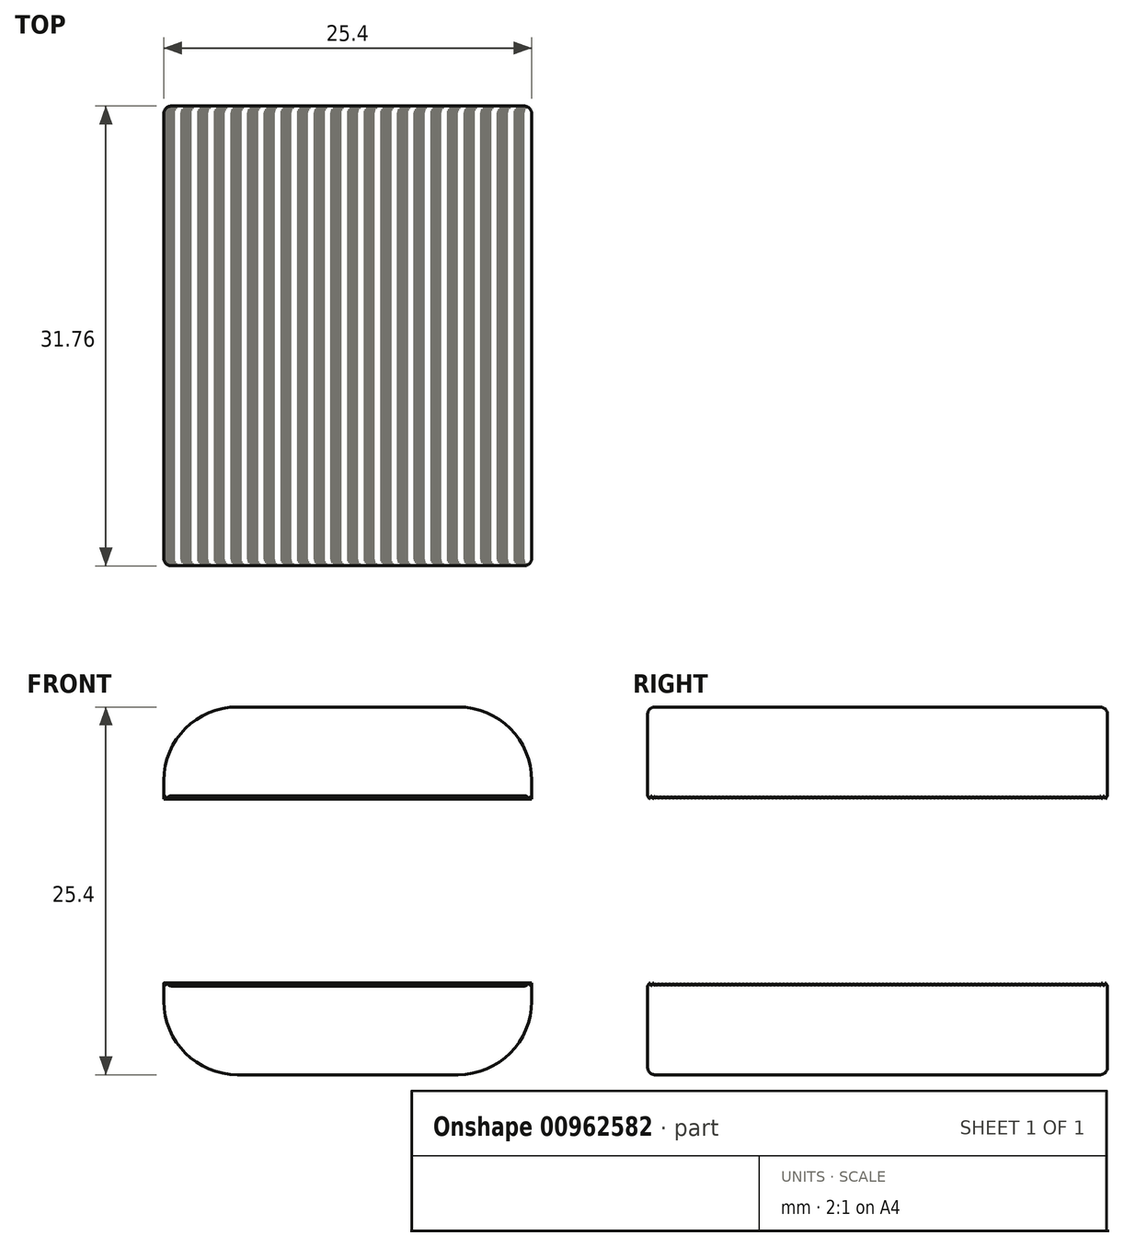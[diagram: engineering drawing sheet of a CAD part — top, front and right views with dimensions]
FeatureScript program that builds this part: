
annotation { "Feature Type Name" : "Feature", "Feature Type Description" : "" }
export const myFeature = defineFeature(function(context is Context, id is Id, definition is map)
    precondition{}
    {
        {
            var Q0;
            Q0=qCreatedBy(makeId("Front.planeOp"),FACE);
            var sketch = newSketch(context, id + "F0", { "sketchPlane" : qUnion([Q0])});
            skLineSegment(sketch, "E0.bottom", {"start": v(12.7, -12.7) * mm, "end": v(-12.7, -12.7) * mm});
            skLineSegment(sketch, "E0.top", {"start": v(12.7, 12.7) * mm, "end": v(-12.7, 12.7) * mm});
            skLineSegment(sketch, "E0.left", {"start": v(12.7, -12.7) * mm, "end": v(12.7, -6.35) * mm});
            skLineSegment(sketch, "E0.right", {"start": v(-12.7, -12.7) * mm, "end": v(-12.7, -6.35) * mm});
            skPoint(sketch, "E0.middle", {"position": v(0, 0) * mm});
            skLineSegment(sketch, "E1.bottom", {"start": v(12.7, -6.35) * mm, "end": v(-12.7, -6.35) * mm});
            skLineSegment(sketch, "E1.top", {"start": v(12.7, 6.35) * mm, "end": v(-12.7, 6.35) * mm});
            skLineSegment(sketch, "E2.trimOffspring", {"start": v(-12.7, 6.35) * mm, "end": v(-12.7, 12.7) * mm});
            skLineSegment(sketch, "E3.trimOffspring", {"start": v(12.7, 6.35) * mm, "end": v(12.7, 12.7) * mm});
            skSolve(sketch);
        }
        {
            var Q0;
            Q0 = qSketchRegion(id + "F0", true);
            extrude(context, id + "F1", {"entities" : qUnion([Q0]), "endBound" : BoundingType.SYMMETRIC, "depth" : 31.75 * mm, "offsetDistance" : 25.4 * mm});
        }
        {
            var Q0;
            Q0=qCreatedBy(makeId("Right.planeOp"),FACE);
            var sketch = newSketch(context, id + "F2", { "sketchPlane" : qUnion([Q0])});
            skLineSegment(sketch, "E4", {"start": v(0, 6.35) * mm, "end": v(-0.13, 6.57) * mm});
            skLineSegment(sketch, "E5", {"start": v(-0.13, 6.57) * mm, "end": v(-0.25, 6.35) * mm});
            skLineSegment(sketch, "E6.1.0.0", {"start": v(-0.25, 6.35) * mm, "end": v(-0.38, 6.57) * mm});
            skLineSegment(sketch, "E6.1.0.1", {"start": v(-0.38, 6.57) * mm, "end": v(-0.5, 6.35) * mm});
            skLineSegment(sketch, "E6.2.0.0", {"start": v(-0.5, 6.35) * mm, "end": v(-0.64, 6.57) * mm});
            skLineSegment(sketch, "E6.2.0.1", {"start": v(-0.64, 6.57) * mm, "end": v(-0.76, 6.35) * mm});
            skLineSegment(sketch, "E6.3.0.0", {"start": v(-0.76, 6.35) * mm, "end": v(-0.89, 6.57) * mm});
            skLineSegment(sketch, "E6.3.0.1", {"start": v(-0.89, 6.57) * mm, "end": v(-1.02, 6.35) * mm});
            skLineSegment(sketch, "E6.4.0.0", {"start": v(-1.02, 6.35) * mm, "end": v(-1.14, 6.57) * mm});
            skLineSegment(sketch, "E6.4.0.1", {"start": v(-1.14, 6.57) * mm, "end": v(-1.27, 6.35) * mm});
            skLineSegment(sketch, "E6.5.0.0", {"start": v(-1.27, 6.35) * mm, "end": v(-1.4, 6.57) * mm});
            skLineSegment(sketch, "E6.5.0.1", {"start": v(-1.4, 6.57) * mm, "end": v(-1.52, 6.35) * mm});
            skLineSegment(sketch, "E6.6.0.0", {"start": v(-1.52, 6.35) * mm, "end": v(-1.65, 6.57) * mm});
            skLineSegment(sketch, "E6.6.0.1", {"start": v(-1.65, 6.57) * mm, "end": v(-1.78, 6.35) * mm});
            skLineSegment(sketch, "E6.7.0.0", {"start": v(-1.78, 6.35) * mm, "end": v(-1.9, 6.57) * mm});
            skLineSegment(sketch, "E6.7.0.1", {"start": v(-1.9, 6.57) * mm, "end": v(-2.03, 6.35) * mm});
            skLineSegment(sketch, "E6.8.0.0", {"start": v(-2.03, 6.35) * mm, "end": v(-2.16, 6.57) * mm});
            skLineSegment(sketch, "E6.8.0.1", {"start": v(-2.16, 6.57) * mm, "end": v(-2.29, 6.35) * mm});
            skLineSegment(sketch, "E6.9.0.0", {"start": v(-2.29, 6.35) * mm, "end": v(-2.41, 6.57) * mm});
            skLineSegment(sketch, "E6.9.0.1", {"start": v(-2.41, 6.57) * mm, "end": v(-2.54, 6.35) * mm});
            skLineSegment(sketch, "E6.10.0.0", {"start": v(-2.54, 6.35) * mm, "end": v(-2.67, 6.57) * mm});
            skLineSegment(sketch, "E6.10.0.1", {"start": v(-2.67, 6.57) * mm, "end": v(-2.8, 6.35) * mm});
            skLineSegment(sketch, "E6.11.0.0", {"start": v(-2.8, 6.35) * mm, "end": v(-2.92, 6.57) * mm});
            skLineSegment(sketch, "E6.11.0.1", {"start": v(-2.92, 6.57) * mm, "end": v(-3.05, 6.35) * mm});
            skLineSegment(sketch, "E6.12.0.0", {"start": v(-3.05, 6.35) * mm, "end": v(-3.18, 6.57) * mm});
            skLineSegment(sketch, "E6.12.0.1", {"start": v(-3.18, 6.57) * mm, "end": v(-3.3, 6.35) * mm});
            skLineSegment(sketch, "E6.13.0.0", {"start": v(-3.3, 6.35) * mm, "end": v(-3.43, 6.57) * mm});
            skLineSegment(sketch, "E6.13.0.1", {"start": v(-3.43, 6.57) * mm, "end": v(-3.56, 6.35) * mm});
            skLineSegment(sketch, "E6.14.0.0", {"start": v(-3.56, 6.35) * mm, "end": v(-3.68, 6.57) * mm});
            skLineSegment(sketch, "E6.14.0.1", {"start": v(-3.68, 6.57) * mm, "end": v(-3.81, 6.35) * mm});
            skLineSegment(sketch, "E6.15.0.0", {"start": v(-3.81, 6.35) * mm, "end": v(-3.94, 6.57) * mm});
            skLineSegment(sketch, "E6.15.0.1", {"start": v(-3.94, 6.57) * mm, "end": v(-4.06, 6.35) * mm});
            skLineSegment(sketch, "E6.16.0.0", {"start": v(-4.06, 6.35) * mm, "end": v(-4.2, 6.57) * mm});
            skLineSegment(sketch, "E6.16.0.1", {"start": v(-4.2, 6.57) * mm, "end": v(-4.32, 6.35) * mm});
            skLineSegment(sketch, "E6.17.0.0", {"start": v(-4.32, 6.35) * mm, "end": v(-4.45, 6.57) * mm});
            skLineSegment(sketch, "E6.17.0.1", {"start": v(-4.45, 6.57) * mm, "end": v(-4.57, 6.35) * mm});
            skLineSegment(sketch, "E6.18.0.0", {"start": v(-4.57, 6.35) * mm, "end": v(-4.7, 6.57) * mm});
            skLineSegment(sketch, "E6.18.0.1", {"start": v(-4.7, 6.57) * mm, "end": v(-4.83, 6.35) * mm});
            skLineSegment(sketch, "E6.19.0.0", {"start": v(-4.83, 6.35) * mm, "end": v(-4.95, 6.57) * mm});
            skLineSegment(sketch, "E6.19.0.1", {"start": v(-4.95, 6.57) * mm, "end": v(-5.08, 6.35) * mm});
            skLineSegment(sketch, "E6.20.0.0", {"start": v(-5.08, 6.35) * mm, "end": v(-5.2, 6.57) * mm});
            skLineSegment(sketch, "E6.20.0.1", {"start": v(-5.2, 6.57) * mm, "end": v(-5.33, 6.35) * mm});
            skLineSegment(sketch, "E6.21.0.0", {"start": v(-5.33, 6.35) * mm, "end": v(-5.46, 6.57) * mm});
            skLineSegment(sketch, "E6.21.0.1", {"start": v(-5.46, 6.57) * mm, "end": v(-5.59, 6.35) * mm});
            skLineSegment(sketch, "E6.22.0.0", {"start": v(-5.59, 6.35) * mm, "end": v(-5.72, 6.57) * mm});
            skLineSegment(sketch, "E6.22.0.1", {"start": v(-5.72, 6.57) * mm, "end": v(-5.84, 6.35) * mm});
            skLineSegment(sketch, "E6.23.0.0", {"start": v(-5.84, 6.35) * mm, "end": v(-5.97, 6.57) * mm});
            skLineSegment(sketch, "E6.23.0.1", {"start": v(-5.97, 6.57) * mm, "end": v(-6.1, 6.35) * mm});
            skLineSegment(sketch, "E6.24.0.0", {"start": v(-6.1, 6.35) * mm, "end": v(-6.22, 6.57) * mm});
            skLineSegment(sketch, "E6.24.0.1", {"start": v(-6.22, 6.57) * mm, "end": v(-6.35, 6.35) * mm});
            skLineSegment(sketch, "E6.direction1", {"start": v(-0.25, 6.35) * mm, "end": v(-0.5, 6.35) * mm, "construction": true});
            skLineSegment(sketch, "E7.0.25.0", {"start": v(-6.35, 6.35) * mm, "end": v(-6.48, 6.57) * mm});
            skLineSegment(sketch, "E7.3.25.0", {"start": v(-6.48, 6.57) * mm, "end": v(-6.6, 6.35) * mm});
            skLineSegment(sketch, "E7.0.26.0", {"start": v(-6.6, 6.35) * mm, "end": v(-6.73, 6.57) * mm});
            skLineSegment(sketch, "E7.3.26.0", {"start": v(-6.73, 6.57) * mm, "end": v(-6.86, 6.35) * mm});
            skLineSegment(sketch, "E7.0.27.0", {"start": v(-6.86, 6.35) * mm, "end": v(-6.99, 6.57) * mm});
            skLineSegment(sketch, "E7.3.27.0", {"start": v(-6.99, 6.57) * mm, "end": v(-7.11, 6.35) * mm});
            skLineSegment(sketch, "E7.0.28.0", {"start": v(-7.11, 6.35) * mm, "end": v(-7.24, 6.57) * mm});
            skLineSegment(sketch, "E7.3.28.0", {"start": v(-7.24, 6.57) * mm, "end": v(-7.37, 6.35) * mm});
            skLineSegment(sketch, "E7.0.29.0", {"start": v(-7.37, 6.35) * mm, "end": v(-7.5, 6.57) * mm});
            skLineSegment(sketch, "E7.3.29.0", {"start": v(-7.5, 6.57) * mm, "end": v(-7.62, 6.35) * mm});
            skLineSegment(sketch, "E7.0.30.0", {"start": v(-7.62, 6.35) * mm, "end": v(-7.75, 6.57) * mm});
            skLineSegment(sketch, "E7.3.30.0", {"start": v(-7.75, 6.57) * mm, "end": v(-7.87, 6.35) * mm});
            skLineSegment(sketch, "E7.0.31.0", {"start": v(-7.87, 6.35) * mm, "end": v(-8, 6.57) * mm});
            skLineSegment(sketch, "E7.3.31.0", {"start": v(-8, 6.57) * mm, "end": v(-8.13, 6.35) * mm});
            skLineSegment(sketch, "E7.0.32.0", {"start": v(-8.13, 6.35) * mm, "end": v(-8.26, 6.57) * mm});
            skLineSegment(sketch, "E7.3.32.0", {"start": v(-8.26, 6.57) * mm, "end": v(-8.38, 6.35) * mm});
            skLineSegment(sketch, "E7.0.33.0", {"start": v(-8.38, 6.35) * mm, "end": v(-8.5, 6.57) * mm});
            skLineSegment(sketch, "E7.3.33.0", {"start": v(-8.5, 6.57) * mm, "end": v(-8.64, 6.35) * mm});
            skLineSegment(sketch, "E7.0.34.0", {"start": v(-8.64, 6.35) * mm, "end": v(-8.76, 6.57) * mm});
            skLineSegment(sketch, "E7.3.34.0", {"start": v(-8.76, 6.57) * mm, "end": v(-8.9, 6.35) * mm});
            skLineSegment(sketch, "E7.0.35.0", {"start": v(-8.9, 6.35) * mm, "end": v(-9.02, 6.57) * mm});
            skLineSegment(sketch, "E7.3.35.0", {"start": v(-9.02, 6.57) * mm, "end": v(-9.14, 6.35) * mm});
            skLineSegment(sketch, "E7.0.36.0", {"start": v(-9.14, 6.35) * mm, "end": v(-9.27, 6.57) * mm});
            skLineSegment(sketch, "E7.3.36.0", {"start": v(-9.27, 6.57) * mm, "end": v(-9.4, 6.35) * mm});
            skLineSegment(sketch, "E7.0.37.0", {"start": v(-9.4, 6.35) * mm, "end": v(-9.53, 6.57) * mm});
            skLineSegment(sketch, "E7.3.37.0", {"start": v(-9.53, 6.57) * mm, "end": v(-9.65, 6.35) * mm});
            skLineSegment(sketch, "E7.0.38.0", {"start": v(-9.65, 6.35) * mm, "end": v(-9.78, 6.57) * mm});
            skLineSegment(sketch, "E7.3.38.0", {"start": v(-9.78, 6.57) * mm, "end": v(-9.9, 6.35) * mm});
            skLineSegment(sketch, "E7.0.39.0", {"start": v(-9.9, 6.35) * mm, "end": v(-10.03, 6.57) * mm});
            skLineSegment(sketch, "E7.3.39.0", {"start": v(-10.03, 6.57) * mm, "end": v(-10.16, 6.35) * mm});
            skLineSegment(sketch, "E8.1.0.0", {"start": v(0.13, 6.57) * mm, "end": v(0, 6.35) * mm});
            skLineSegment(sketch, "E8.1.0.1", {"start": v(0.25, 6.35) * mm, "end": v(0.13, 6.57) * mm});
            skLineSegment(sketch, "E8.2.0.0", {"start": v(0.38, 6.57) * mm, "end": v(0.25, 6.35) * mm});
            skLineSegment(sketch, "E8.2.0.1", {"start": v(0.5, 6.35) * mm, "end": v(0.38, 6.57) * mm});
            skLineSegment(sketch, "E8.3.0.0", {"start": v(0.64, 6.57) * mm, "end": v(0.5, 6.35) * mm});
            skLineSegment(sketch, "E8.3.0.1", {"start": v(0.76, 6.35) * mm, "end": v(0.63, 6.57) * mm});
            skLineSegment(sketch, "E8.4.0.0", {"start": v(0.89, 6.57) * mm, "end": v(0.76, 6.35) * mm});
            skLineSegment(sketch, "E8.4.0.1", {"start": v(1.02, 6.35) * mm, "end": v(0.89, 6.57) * mm});
            skLineSegment(sketch, "E8.5.0.0", {"start": v(1.14, 6.57) * mm, "end": v(1.02, 6.35) * mm});
            skLineSegment(sketch, "E8.5.0.1", {"start": v(1.27, 6.35) * mm, "end": v(1.14, 6.57) * mm});
            skLineSegment(sketch, "E8.6.0.0", {"start": v(1.4, 6.57) * mm, "end": v(1.27, 6.35) * mm});
            skLineSegment(sketch, "E8.6.0.1", {"start": v(1.52, 6.35) * mm, "end": v(1.4, 6.57) * mm});
            skLineSegment(sketch, "E8.7.0.0", {"start": v(1.65, 6.57) * mm, "end": v(1.52, 6.35) * mm});
            skLineSegment(sketch, "E8.7.0.1", {"start": v(1.78, 6.35) * mm, "end": v(1.65, 6.57) * mm});
            skLineSegment(sketch, "E8.8.0.0", {"start": v(1.9, 6.57) * mm, "end": v(1.78, 6.35) * mm});
            skLineSegment(sketch, "E8.8.0.1", {"start": v(2.03, 6.35) * mm, "end": v(1.9, 6.57) * mm});
            skLineSegment(sketch, "E8.9.0.0", {"start": v(2.16, 6.57) * mm, "end": v(2.03, 6.35) * mm});
            skLineSegment(sketch, "E8.9.0.1", {"start": v(2.29, 6.35) * mm, "end": v(2.16, 6.57) * mm});
            skLineSegment(sketch, "E8.10.0.0", {"start": v(2.41, 6.57) * mm, "end": v(2.29, 6.35) * mm});
            skLineSegment(sketch, "E8.10.0.1", {"start": v(2.54, 6.35) * mm, "end": v(2.41, 6.57) * mm});
            skLineSegment(sketch, "E8.11.0.0", {"start": v(2.67, 6.57) * mm, "end": v(2.54, 6.35) * mm});
            skLineSegment(sketch, "E8.11.0.1", {"start": v(2.8, 6.35) * mm, "end": v(2.67, 6.57) * mm});
            skLineSegment(sketch, "E8.12.0.0", {"start": v(2.92, 6.57) * mm, "end": v(2.8, 6.35) * mm});
            skLineSegment(sketch, "E8.12.0.1", {"start": v(3.05, 6.35) * mm, "end": v(2.92, 6.57) * mm});
            skLineSegment(sketch, "E8.13.0.0", {"start": v(3.18, 6.57) * mm, "end": v(3.05, 6.35) * mm});
            skLineSegment(sketch, "E8.13.0.1", {"start": v(3.3, 6.35) * mm, "end": v(3.18, 6.57) * mm});
            skLineSegment(sketch, "E8.14.0.0", {"start": v(3.43, 6.57) * mm, "end": v(3.3, 6.35) * mm});
            skLineSegment(sketch, "E8.14.0.1", {"start": v(3.56, 6.35) * mm, "end": v(3.43, 6.57) * mm});
            skLineSegment(sketch, "E8.15.0.0", {"start": v(3.68, 6.57) * mm, "end": v(3.56, 6.35) * mm});
            skLineSegment(sketch, "E8.15.0.1", {"start": v(3.81, 6.35) * mm, "end": v(3.68, 6.57) * mm});
            skLineSegment(sketch, "E8.16.0.0", {"start": v(3.94, 6.57) * mm, "end": v(3.81, 6.35) * mm});
            skLineSegment(sketch, "E8.16.0.1", {"start": v(4.06, 6.35) * mm, "end": v(3.94, 6.57) * mm});
            skLineSegment(sketch, "E8.17.0.0", {"start": v(4.2, 6.57) * mm, "end": v(4.06, 6.35) * mm});
            skLineSegment(sketch, "E8.17.0.1", {"start": v(4.32, 6.35) * mm, "end": v(4.2, 6.57) * mm});
            skLineSegment(sketch, "E8.18.0.0", {"start": v(4.45, 6.57) * mm, "end": v(4.32, 6.35) * mm});
            skLineSegment(sketch, "E8.18.0.1", {"start": v(4.57, 6.35) * mm, "end": v(4.45, 6.57) * mm});
            skLineSegment(sketch, "E8.19.0.0", {"start": v(4.7, 6.57) * mm, "end": v(4.57, 6.35) * mm});
            skLineSegment(sketch, "E8.19.0.1", {"start": v(4.83, 6.35) * mm, "end": v(4.7, 6.57) * mm});
            skLineSegment(sketch, "E8.20.0.0", {"start": v(4.95, 6.57) * mm, "end": v(4.83, 6.35) * mm});
            skLineSegment(sketch, "E8.20.0.1", {"start": v(5.08, 6.35) * mm, "end": v(4.95, 6.57) * mm});
            skLineSegment(sketch, "E8.21.0.0", {"start": v(5.2, 6.57) * mm, "end": v(5.08, 6.35) * mm});
            skLineSegment(sketch, "E8.21.0.1", {"start": v(5.33, 6.35) * mm, "end": v(5.2, 6.57) * mm});
            skLineSegment(sketch, "E8.22.0.0", {"start": v(5.46, 6.57) * mm, "end": v(5.33, 6.35) * mm});
            skLineSegment(sketch, "E8.22.0.1", {"start": v(5.59, 6.35) * mm, "end": v(5.46, 6.57) * mm});
            skLineSegment(sketch, "E8.23.0.0", {"start": v(5.72, 6.57) * mm, "end": v(5.59, 6.35) * mm});
            skLineSegment(sketch, "E8.23.0.1", {"start": v(5.84, 6.35) * mm, "end": v(5.72, 6.57) * mm});
            skLineSegment(sketch, "E8.24.0.0", {"start": v(5.97, 6.57) * mm, "end": v(5.84, 6.35) * mm});
            skLineSegment(sketch, "E8.24.0.1", {"start": v(6.1, 6.35) * mm, "end": v(5.97, 6.57) * mm});
            skLineSegment(sketch, "E8.25.0.0", {"start": v(6.22, 6.57) * mm, "end": v(6.1, 6.35) * mm});
            skLineSegment(sketch, "E8.25.0.1", {"start": v(6.35, 6.35) * mm, "end": v(6.22, 6.57) * mm});
            skLineSegment(sketch, "E8.26.0.0", {"start": v(6.48, 6.57) * mm, "end": v(6.35, 6.35) * mm});
            skLineSegment(sketch, "E8.26.0.1", {"start": v(6.6, 6.35) * mm, "end": v(6.48, 6.57) * mm});
            skLineSegment(sketch, "E8.27.0.0", {"start": v(6.73, 6.57) * mm, "end": v(6.6, 6.35) * mm});
            skLineSegment(sketch, "E8.27.0.1", {"start": v(6.86, 6.35) * mm, "end": v(6.73, 6.57) * mm});
            skLineSegment(sketch, "E8.28.0.0", {"start": v(6.99, 6.57) * mm, "end": v(6.86, 6.35) * mm});
            skLineSegment(sketch, "E8.28.0.1", {"start": v(7.11, 6.35) * mm, "end": v(6.99, 6.57) * mm});
            skLineSegment(sketch, "E8.29.0.0", {"start": v(7.24, 6.57) * mm, "end": v(7.11, 6.35) * mm});
            skLineSegment(sketch, "E8.29.0.1", {"start": v(7.37, 6.35) * mm, "end": v(7.24, 6.57) * mm});
            skLineSegment(sketch, "E8.30.0.0", {"start": v(7.5, 6.57) * mm, "end": v(7.37, 6.35) * mm});
            skLineSegment(sketch, "E8.30.0.1", {"start": v(7.62, 6.35) * mm, "end": v(7.5, 6.57) * mm});
            skLineSegment(sketch, "E8.31.0.0", {"start": v(7.75, 6.57) * mm, "end": v(7.62, 6.35) * mm});
            skLineSegment(sketch, "E8.31.0.1", {"start": v(7.87, 6.35) * mm, "end": v(7.75, 6.57) * mm});
            skLineSegment(sketch, "E8.32.0.0", {"start": v(8, 6.57) * mm, "end": v(7.87, 6.35) * mm});
            skLineSegment(sketch, "E8.32.0.1", {"start": v(8.13, 6.35) * mm, "end": v(8, 6.57) * mm});
            skLineSegment(sketch, "E8.33.0.0", {"start": v(8.26, 6.57) * mm, "end": v(8.13, 6.35) * mm});
            skLineSegment(sketch, "E8.33.0.1", {"start": v(8.38, 6.35) * mm, "end": v(8.26, 6.57) * mm});
            skLineSegment(sketch, "E8.34.0.0", {"start": v(8.5, 6.57) * mm, "end": v(8.38, 6.35) * mm});
            skLineSegment(sketch, "E8.34.0.1", {"start": v(8.64, 6.35) * mm, "end": v(8.5, 6.57) * mm});
            skLineSegment(sketch, "E8.35.0.0", {"start": v(8.76, 6.57) * mm, "end": v(8.64, 6.35) * mm});
            skLineSegment(sketch, "E8.35.0.1", {"start": v(8.9, 6.35) * mm, "end": v(8.76, 6.57) * mm});
            skLineSegment(sketch, "E8.36.0.0", {"start": v(9.02, 6.57) * mm, "end": v(8.9, 6.35) * mm});
            skLineSegment(sketch, "E8.36.0.1", {"start": v(9.14, 6.35) * mm, "end": v(9.02, 6.57) * mm});
            skLineSegment(sketch, "E8.37.0.0", {"start": v(9.27, 6.57) * mm, "end": v(9.14, 6.35) * mm});
            skLineSegment(sketch, "E8.37.0.1", {"start": v(9.4, 6.35) * mm, "end": v(9.27, 6.57) * mm});
            skLineSegment(sketch, "E8.38.0.0", {"start": v(9.53, 6.57) * mm, "end": v(9.4, 6.35) * mm});
            skLineSegment(sketch, "E8.38.0.1", {"start": v(9.65, 6.35) * mm, "end": v(9.53, 6.57) * mm});
            skLineSegment(sketch, "E8.39.0.0", {"start": v(9.78, 6.57) * mm, "end": v(9.65, 6.35) * mm});
            skLineSegment(sketch, "E8.39.0.1", {"start": v(9.9, 6.35) * mm, "end": v(9.78, 6.57) * mm});
            skLineSegment(sketch, "E8.40.0.0", {"start": v(10.03, 6.57) * mm, "end": v(9.9, 6.35) * mm});
            skLineSegment(sketch, "E8.40.0.1", {"start": v(10.16, 6.35) * mm, "end": v(10.03, 6.57) * mm});
            skLineSegment(sketch, "E8.direction1", {"start": v(-0.25, 6.35) * mm, "end": v(0, 6.35) * mm, "construction": true});
            skLineSegment(sketch, "E9.0.41.0", {"start": v(10.29, 6.57) * mm, "end": v(10.16, 6.35) * mm});
            skLineSegment(sketch, "E9.3.41.0", {"start": v(10.41, 6.35) * mm, "end": v(10.29, 6.57) * mm});
            skLineSegment(sketch, "E9.0.42.0", {"start": v(10.54, 6.57) * mm, "end": v(10.41, 6.35) * mm});
            skLineSegment(sketch, "E9.3.42.0", {"start": v(10.67, 6.35) * mm, "end": v(10.54, 6.57) * mm});
            skLineSegment(sketch, "E9.0.43.0", {"start": v(10.8, 6.57) * mm, "end": v(10.67, 6.35) * mm});
            skLineSegment(sketch, "E9.3.43.0", {"start": v(10.92, 6.35) * mm, "end": v(10.8, 6.57) * mm});
            skLineSegment(sketch, "E9.0.44.0", {"start": v(11.05, 6.57) * mm, "end": v(10.92, 6.35) * mm});
            skLineSegment(sketch, "E9.3.44.0", {"start": v(11.18, 6.35) * mm, "end": v(11.05, 6.57) * mm});
            skLineSegment(sketch, "E9.0.45.0", {"start": v(11.3, 6.57) * mm, "end": v(11.18, 6.35) * mm});
            skLineSegment(sketch, "E9.3.45.0", {"start": v(11.43, 6.35) * mm, "end": v(11.3, 6.57) * mm});
            skLineSegment(sketch, "E9.0.46.0", {"start": v(11.56, 6.57) * mm, "end": v(11.43, 6.35) * mm});
            skLineSegment(sketch, "E9.3.46.0", {"start": v(11.68, 6.35) * mm, "end": v(11.56, 6.57) * mm});
            skLineSegment(sketch, "E9.0.47.0", {"start": v(11.81, 6.57) * mm, "end": v(11.68, 6.35) * mm});
            skLineSegment(sketch, "E9.3.47.0", {"start": v(11.94, 6.35) * mm, "end": v(11.81, 6.57) * mm});
            skLineSegment(sketch, "E9.0.48.0", {"start": v(12.07, 6.57) * mm, "end": v(11.94, 6.35) * mm});
            skLineSegment(sketch, "E9.3.48.0", {"start": v(12.2, 6.35) * mm, "end": v(12.07, 6.57) * mm});
            skLineSegment(sketch, "E9.0.49.0", {"start": v(12.32, 6.57) * mm, "end": v(12.2, 6.35) * mm});
            skLineSegment(sketch, "E9.3.49.0", {"start": v(12.45, 6.35) * mm, "end": v(12.32, 6.57) * mm});
            skLineSegment(sketch, "E9.0.50.0", {"start": v(12.57, 6.57) * mm, "end": v(12.45, 6.35) * mm});
            skLineSegment(sketch, "E9.3.50.0", {"start": v(12.7, 6.35) * mm, "end": v(12.57, 6.57) * mm});
            skLineSegment(sketch, "E9.0.51.0", {"start": v(12.83, 6.57) * mm, "end": v(12.7, 6.35) * mm});
            skLineSegment(sketch, "E9.3.51.0", {"start": v(12.95, 6.35) * mm, "end": v(12.83, 6.57) * mm});
            skLineSegment(sketch, "E9.0.52.0", {"start": v(13.08, 6.57) * mm, "end": v(12.95, 6.35) * mm});
            skLineSegment(sketch, "E9.3.52.0", {"start": v(13.2, 6.35) * mm, "end": v(13.08, 6.57) * mm});
            skLineSegment(sketch, "E9.0.53.0", {"start": v(13.34, 6.57) * mm, "end": v(13.2, 6.35) * mm});
            skLineSegment(sketch, "E9.3.53.0", {"start": v(13.46, 6.35) * mm, "end": v(13.34, 6.57) * mm});
            skLineSegment(sketch, "E9.0.54.0", {"start": v(13.59, 6.57) * mm, "end": v(13.46, 6.35) * mm});
            skLineSegment(sketch, "E9.3.54.0", {"start": v(13.72, 6.35) * mm, "end": v(13.59, 6.57) * mm});
            skLineSegment(sketch, "E9.0.55.0", {"start": v(13.84, 6.57) * mm, "end": v(13.72, 6.35) * mm});
            skLineSegment(sketch, "E9.3.55.0", {"start": v(13.97, 6.35) * mm, "end": v(13.84, 6.57) * mm});
            skLineSegment(sketch, "E9.0.56.0", {"start": v(14.1, 6.57) * mm, "end": v(13.97, 6.35) * mm});
            skLineSegment(sketch, "E9.3.56.0", {"start": v(14.22, 6.35) * mm, "end": v(14.1, 6.57) * mm});
            skLineSegment(sketch, "E9.0.57.0", {"start": v(14.35, 6.57) * mm, "end": v(14.22, 6.35) * mm});
            skLineSegment(sketch, "E9.3.57.0", {"start": v(14.48, 6.35) * mm, "end": v(14.35, 6.57) * mm});
            skLineSegment(sketch, "E9.0.58.0", {"start": v(14.6, 6.57) * mm, "end": v(14.48, 6.35) * mm});
            skLineSegment(sketch, "E9.3.58.0", {"start": v(14.73, 6.35) * mm, "end": v(14.6, 6.57) * mm});
            skLineSegment(sketch, "E9.0.59.0", {"start": v(14.86, 6.57) * mm, "end": v(14.73, 6.35) * mm});
            skLineSegment(sketch, "E9.3.59.0", {"start": v(14.99, 6.35) * mm, "end": v(14.86, 6.57) * mm});
            skLineSegment(sketch, "E9.0.60.0", {"start": v(15.11, 6.57) * mm, "end": v(14.99, 6.35) * mm});
            skLineSegment(sketch, "E9.3.60.0", {"start": v(15.24, 6.35) * mm, "end": v(15.11, 6.57) * mm});
            skLineSegment(sketch, "E9.0.61.0", {"start": v(15.37, 6.57) * mm, "end": v(15.24, 6.35) * mm});
            skLineSegment(sketch, "E9.3.61.0", {"start": v(15.5, 6.35) * mm, "end": v(15.37, 6.57) * mm});
            skLineSegment(sketch, "E10.0.40.0", {"start": v(-10.16, 6.35) * mm, "end": v(-10.29, 6.57) * mm});
            skLineSegment(sketch, "E10.3.40.0", {"start": v(-10.29, 6.57) * mm, "end": v(-10.41, 6.35) * mm});
            skLineSegment(sketch, "E10.0.41.0", {"start": v(-10.41, 6.35) * mm, "end": v(-10.54, 6.57) * mm});
            skLineSegment(sketch, "E10.3.41.0", {"start": v(-10.54, 6.57) * mm, "end": v(-10.67, 6.35) * mm});
            skLineSegment(sketch, "E10.0.42.0", {"start": v(-10.67, 6.35) * mm, "end": v(-10.8, 6.57) * mm});
            skLineSegment(sketch, "E10.3.42.0", {"start": v(-10.8, 6.57) * mm, "end": v(-10.92, 6.35) * mm});
            skLineSegment(sketch, "E10.0.43.0", {"start": v(-10.92, 6.35) * mm, "end": v(-11.05, 6.57) * mm});
            skLineSegment(sketch, "E10.3.43.0", {"start": v(-11.05, 6.57) * mm, "end": v(-11.18, 6.35) * mm});
            skLineSegment(sketch, "E10.0.44.0", {"start": v(-11.18, 6.35) * mm, "end": v(-11.3, 6.57) * mm});
            skLineSegment(sketch, "E10.3.44.0", {"start": v(-11.3, 6.57) * mm, "end": v(-11.43, 6.35) * mm});
            skLineSegment(sketch, "E10.0.45.0", {"start": v(-11.43, 6.35) * mm, "end": v(-11.56, 6.57) * mm});
            skLineSegment(sketch, "E10.3.45.0", {"start": v(-11.56, 6.57) * mm, "end": v(-11.68, 6.35) * mm});
            skLineSegment(sketch, "E10.0.46.0", {"start": v(-11.68, 6.35) * mm, "end": v(-11.81, 6.57) * mm});
            skLineSegment(sketch, "E10.3.46.0", {"start": v(-11.81, 6.57) * mm, "end": v(-11.94, 6.35) * mm});
            skLineSegment(sketch, "E10.0.47.0", {"start": v(-11.94, 6.35) * mm, "end": v(-12.07, 6.57) * mm});
            skLineSegment(sketch, "E10.3.47.0", {"start": v(-12.07, 6.57) * mm, "end": v(-12.2, 6.35) * mm});
            skLineSegment(sketch, "E10.0.48.0", {"start": v(-12.2, 6.35) * mm, "end": v(-12.32, 6.57) * mm});
            skLineSegment(sketch, "E10.3.48.0", {"start": v(-12.32, 6.57) * mm, "end": v(-12.45, 6.35) * mm});
            skLineSegment(sketch, "E10.0.49.0", {"start": v(-12.45, 6.35) * mm, "end": v(-12.57, 6.57) * mm});
            skLineSegment(sketch, "E10.3.49.0", {"start": v(-12.57, 6.57) * mm, "end": v(-12.7, 6.35) * mm});
            skLineSegment(sketch, "E10.0.50.0", {"start": v(-12.7, 6.35) * mm, "end": v(-12.83, 6.57) * mm});
            skLineSegment(sketch, "E10.3.50.0", {"start": v(-12.83, 6.57) * mm, "end": v(-12.95, 6.35) * mm});
            skLineSegment(sketch, "E10.0.51.0", {"start": v(-12.95, 6.35) * mm, "end": v(-13.08, 6.57) * mm});
            skLineSegment(sketch, "E10.3.51.0", {"start": v(-13.08, 6.57) * mm, "end": v(-13.2, 6.35) * mm});
            skLineSegment(sketch, "E10.0.52.0", {"start": v(-13.2, 6.35) * mm, "end": v(-13.34, 6.57) * mm});
            skLineSegment(sketch, "E10.3.52.0", {"start": v(-13.34, 6.57) * mm, "end": v(-13.46, 6.35) * mm});
            skLineSegment(sketch, "E10.0.53.0", {"start": v(-13.46, 6.35) * mm, "end": v(-13.59, 6.57) * mm});
            skLineSegment(sketch, "E10.3.53.0", {"start": v(-13.59, 6.57) * mm, "end": v(-13.72, 6.35) * mm});
            skLineSegment(sketch, "E10.0.54.0", {"start": v(-13.72, 6.35) * mm, "end": v(-13.84, 6.57) * mm});
            skLineSegment(sketch, "E10.3.54.0", {"start": v(-13.84, 6.57) * mm, "end": v(-13.97, 6.35) * mm});
            skLineSegment(sketch, "E10.0.55.0", {"start": v(-13.97, 6.35) * mm, "end": v(-14.1, 6.57) * mm});
            skLineSegment(sketch, "E10.3.55.0", {"start": v(-14.1, 6.57) * mm, "end": v(-14.22, 6.35) * mm});
            skLineSegment(sketch, "E10.0.56.0", {"start": v(-14.22, 6.35) * mm, "end": v(-14.35, 6.57) * mm});
            skLineSegment(sketch, "E10.3.56.0", {"start": v(-14.35, 6.57) * mm, "end": v(-14.48, 6.35) * mm});
            skLineSegment(sketch, "E10.0.57.0", {"start": v(-14.48, 6.35) * mm, "end": v(-14.6, 6.57) * mm});
            skLineSegment(sketch, "E10.3.57.0", {"start": v(-14.6, 6.57) * mm, "end": v(-14.73, 6.35) * mm});
            skLineSegment(sketch, "E10.0.58.0", {"start": v(-14.73, 6.35) * mm, "end": v(-14.86, 6.57) * mm});
            skLineSegment(sketch, "E10.3.58.0", {"start": v(-14.86, 6.57) * mm, "end": v(-14.99, 6.35) * mm});
            skLineSegment(sketch, "E10.0.59.0", {"start": v(-14.99, 6.35) * mm, "end": v(-15.11, 6.57) * mm});
            skLineSegment(sketch, "E10.3.59.0", {"start": v(-15.11, 6.57) * mm, "end": v(-15.24, 6.35) * mm});
            skLineSegment(sketch, "E10.0.60.0", {"start": v(-15.24, 6.35) * mm, "end": v(-15.37, 6.57) * mm});
            skLineSegment(sketch, "E10.3.60.0", {"start": v(-15.37, 6.57) * mm, "end": v(-15.5, 6.35) * mm});
            skLineSegment(sketch, "E10.0.61.0", {"start": v(-15.5, 6.35) * mm, "end": v(-15.62, 6.57) * mm});
            skLineSegment(sketch, "E10.3.61.0", {"start": v(-15.62, 6.57) * mm, "end": v(-15.75, 6.35) * mm});
            skLineSegment(sketch, "E10.0.62.0", {"start": v(-15.75, 6.35) * mm, "end": v(-15.88, 6.57) * mm});
            skLineSegment(sketch, "E10.3.62.0", {"start": v(-15.88, 6.57) * mm, "end": v(-16, 6.35) * mm});
            skLineSegment(sketch, "E10.0.63.0", {"start": v(-16, 6.35) * mm, "end": v(-16.13, 6.57) * mm});
            skLineSegment(sketch, "E10.3.63.0", {"start": v(-16.13, 6.57) * mm, "end": v(-16.26, 6.35) * mm});
            skLineSegment(sketch, "E11.0.62.0", {"start": v(15.62, 6.57) * mm, "end": v(15.5, 6.35) * mm});
            skLineSegment(sketch, "E11.3.62.0", {"start": v(15.75, 6.35) * mm, "end": v(15.62, 6.57) * mm});
            skLineSegment(sketch, "E12.0.63.0", {"start": v(15.88, 6.57) * mm, "end": v(15.75, 6.35) * mm});
            skLineSegment(sketch, "E12.3.63.0", {"start": v(16, 6.35) * mm, "end": v(15.88, 6.57) * mm});
            skLineSegment(sketch, "E12.0.64.0", {"start": v(16.13, 6.57) * mm, "end": v(16, 6.35) * mm});
            skLineSegment(sketch, "E12.3.64.0", {"start": v(16.26, 6.35) * mm, "end": v(16.13, 6.57) * mm});
            skLineSegment(sketch, "E13", {"start": v(-16.26, 6.35) * mm, "end": v(-16.26, 6.1) * mm});
            skLineSegment(sketch, "E14", {"start": v(-16.26, 6.1) * mm, "end": v(16.26, 6.1) * mm});
            skLineSegment(sketch, "E15", {"start": v(16.26, 6.1) * mm, "end": v(16.26, 6.35) * mm});
            skLineSegment(sketch, "E16.MirrorCS", {"start": v(9.78, -6.57) * mm, "end": v(9.65, -6.35) * mm});
            skLineSegment(sketch, "E17.MirrorCS", {"start": v(0, -6.35) * mm, "end": v(-0.13, -6.57) * mm});
            skLineSegment(sketch, "E18.MirrorCS", {"start": v(1.4, -6.57) * mm, "end": v(1.27, -6.35) * mm});
            skLineSegment(sketch, "E19.MirrorCS", {"start": v(9.53, -6.57) * mm, "end": v(9.4, -6.35) * mm});
            skLineSegment(sketch, "E20.MirrorCS", {"start": v(-14.35, -6.57) * mm, "end": v(-14.48, -6.35) * mm});
            skLineSegment(sketch, "E21.MirrorCS", {"start": v(-0.5, -6.35) * mm, "end": v(-0.64, -6.57) * mm});
            skLineSegment(sketch, "E22.MirrorCS", {"start": v(0.5, -6.35) * mm, "end": v(0.38, -6.57) * mm});
            skLineSegment(sketch, "E23.MirrorCS", {"start": v(1.65, -6.57) * mm, "end": v(1.52, -6.35) * mm});
            skLineSegment(sketch, "E24.MirrorCS", {"start": v(-14.1, -6.57) * mm, "end": v(-14.22, -6.35) * mm});
            skLineSegment(sketch, "E25.MirrorCS", {"start": v(2.54, -6.35) * mm, "end": v(2.41, -6.57) * mm});
            skLineSegment(sketch, "E26.MirrorCS", {"start": v(1.27, -6.35) * mm, "end": v(1.14, -6.57) * mm});
            skLineSegment(sketch, "E27.MirrorCS", {"start": v(-6.1, -6.35) * mm, "end": v(-6.22, -6.57) * mm});
            skLineSegment(sketch, "E28.MirrorCS", {"start": v(10.16, -6.35) * mm, "end": v(10.03, -6.57) * mm});
            skLineSegment(sketch, "E29.MirrorCS", {"start": v(-0.25, -6.35) * mm, "end": v(0, -6.35) * mm, "construction": true});
            skLineSegment(sketch, "E30.MirrorCS", {"start": v(-0.25, -6.35) * mm, "end": v(-0.5, -6.35) * mm, "construction": true});
            skLineSegment(sketch, "E31.MirrorCS", {"start": v(-8.5, -6.57) * mm, "end": v(-8.64, -6.35) * mm});
            skLineSegment(sketch, "E32.MirrorCS", {"start": v(2.8, -6.35) * mm, "end": v(2.67, -6.57) * mm});
            skLineSegment(sketch, "E33.MirrorCS", {"start": v(0.38, -6.57) * mm, "end": v(0.25, -6.35) * mm});
            skLineSegment(sketch, "E34.MirrorCS", {"start": v(1.14, -6.57) * mm, "end": v(1.02, -6.35) * mm});
            skLineSegment(sketch, "E35.MirrorCS", {"start": v(-2.03, -6.35) * mm, "end": v(-2.16, -6.57) * mm});
            skLineSegment(sketch, "E36.MirrorCS", {"start": v(2.29, -6.35) * mm, "end": v(2.16, -6.57) * mm});
            skLineSegment(sketch, "E37.MirrorCS", {"start": v(-13.97, -6.35) * mm, "end": v(-14.1, -6.57) * mm});
            skLineSegment(sketch, "E38.MirrorCS", {"start": v(-0.25, -6.35) * mm, "end": v(-0.38, -6.57) * mm});
            skLineSegment(sketch, "E39.MirrorCS", {"start": v(13.46, -6.35) * mm, "end": v(13.34, -6.57) * mm});
            skLineSegment(sketch, "E40.MirrorCS", {"start": v(1.52, -6.35) * mm, "end": v(1.4, -6.57) * mm});
            skLineSegment(sketch, "E41.MirrorCS", {"start": v(-0.38, -6.57) * mm, "end": v(-0.5, -6.35) * mm});
            skLineSegment(sketch, "E42.MirrorCS", {"start": v(-12.32, -6.57) * mm, "end": v(-12.45, -6.35) * mm});
            skLineSegment(sketch, "E43.MirrorCS", {"start": v(4.57, -6.35) * mm, "end": v(4.45, -6.57) * mm});
            skLineSegment(sketch, "E44.MirrorCS", {"start": v(-12.07, -6.57) * mm, "end": v(-12.2, -6.35) * mm});
            skLineSegment(sketch, "E45.MirrorCS", {"start": v(8.64, -6.35) * mm, "end": v(8.5, -6.57) * mm});
            skLineSegment(sketch, "E46.MirrorCS", {"start": v(-5.72, -6.57) * mm, "end": v(-5.84, -6.35) * mm});
            skLineSegment(sketch, "E47.MirrorCS", {"start": v(0.89, -6.57) * mm, "end": v(0.76, -6.35) * mm});
            skLineSegment(sketch, "E48.MirrorCS", {"start": v(-4.57, -6.35) * mm, "end": v(-4.7, -6.57) * mm});
            skLineSegment(sketch, "E49.MirrorCS", {"start": v(-6.48, -6.57) * mm, "end": v(-6.6, -6.35) * mm});
            skLineSegment(sketch, "E50.MirrorCS", {"start": v(5.72, -6.57) * mm, "end": v(5.59, -6.35) * mm});
            skLineSegment(sketch, "E51.MirrorCS", {"start": v(15.75, -6.35) * mm, "end": v(15.62, -6.57) * mm});
            skLineSegment(sketch, "E52.MirrorCS", {"start": v(7.75, -6.57) * mm, "end": v(7.62, -6.35) * mm});
            skLineSegment(sketch, "E53.MirrorCS", {"start": v(2.92, -6.57) * mm, "end": v(2.8, -6.35) * mm});
            skLineSegment(sketch, "E54.MirrorCS", {"start": v(0.25, -6.35) * mm, "end": v(0.13, -6.57) * mm});
            skLineSegment(sketch, "E55.MirrorCS", {"start": v(-7.62, -6.35) * mm, "end": v(-7.75, -6.57) * mm});
            skLineSegment(sketch, "E56.MirrorCS", {"start": v(9.65, -6.35) * mm, "end": v(9.53, -6.57) * mm});
            skLineSegment(sketch, "E57.MirrorCS", {"start": v(7.5, -6.57) * mm, "end": v(7.37, -6.35) * mm});
            skLineSegment(sketch, "E58.MirrorCS", {"start": v(2.41, -6.57) * mm, "end": v(2.29, -6.35) * mm});
            skLineSegment(sketch, "E59.MirrorCS", {"start": v(-13.84, -6.57) * mm, "end": v(-13.97, -6.35) * mm});
            skLineSegment(sketch, "E60.MirrorCS", {"start": v(0.64, -6.57) * mm, "end": v(0.5, -6.35) * mm});
            skLineSegment(sketch, "E61.MirrorCS", {"start": v(-4.06, -6.35) * mm, "end": v(-4.2, -6.57) * mm});
            skLineSegment(sketch, "E62.MirrorCS", {"start": v(13.72, -6.35) * mm, "end": v(13.59, -6.57) * mm});
            skLineSegment(sketch, "E63.MirrorCS", {"start": v(2.67, -6.57) * mm, "end": v(2.54, -6.35) * mm});
            skLineSegment(sketch, "E64.MirrorCS", {"start": v(9.9, -6.35) * mm, "end": v(9.78, -6.57) * mm});
            skLineSegment(sketch, "E65.MirrorCS", {"start": v(-7.37, -6.35) * mm, "end": v(-7.5, -6.57) * mm});
            skLineSegment(sketch, "E66.MirrorCS", {"start": v(-14.22, -6.35) * mm, "end": v(-14.35, -6.57) * mm});
            skLineSegment(sketch, "E67.MirrorCS", {"start": v(-3.68, -6.57) * mm, "end": v(-3.81, -6.35) * mm});
            skLineSegment(sketch, "E68.MirrorCS", {"start": v(-2.54, -6.35) * mm, "end": v(-2.67, -6.57) * mm});
            skLineSegment(sketch, "E69.MirrorCS", {"start": v(12.57, -6.57) * mm, "end": v(12.45, -6.35) * mm});
            skLineSegment(sketch, "E70.MirrorCS", {"start": v(-11.18, -6.35) * mm, "end": v(-11.3, -6.57) * mm});
            skLineSegment(sketch, "E71.MirrorCS", {"start": v(15.5, -6.35) * mm, "end": v(15.37, -6.57) * mm});
            skLineSegment(sketch, "E72.MirrorCS", {"start": v(3.43, -6.57) * mm, "end": v(3.3, -6.35) * mm});
            skLineSegment(sketch, "E73.MirrorCS", {"start": v(-0.64, -6.57) * mm, "end": v(-0.76, -6.35) * mm});
            skLineSegment(sketch, "E74.MirrorCS", {"start": v(-14.48, -6.35) * mm, "end": v(-14.6, -6.57) * mm});
            skLineSegment(sketch, "E75.MirrorCS", {"start": v(-10.29, -6.57) * mm, "end": v(-10.41, -6.35) * mm});
            skLineSegment(sketch, "E76.MirrorCS", {"start": v(3.68, -6.57) * mm, "end": v(3.56, -6.35) * mm});
            skLineSegment(sketch, "E77.MirrorCS", {"start": v(-3.43, -6.57) * mm, "end": v(-3.56, -6.35) * mm});
            skLineSegment(sketch, "E78.MirrorCS", {"start": v(-9.4, -6.35) * mm, "end": v(-9.53, -6.57) * mm});
            skLineSegment(sketch, "E79.MirrorCS", {"start": v(0.76, -6.35) * mm, "end": v(0.63, -6.57) * mm});
            skLineSegment(sketch, "E80.MirrorCS", {"start": v(5.46, -6.57) * mm, "end": v(5.33, -6.35) * mm});
            skLineSegment(sketch, "E81.MirrorCS", {"start": v(10.03, -6.57) * mm, "end": v(9.9, -6.35) * mm});
            skLineSegment(sketch, "E82.MirrorCS", {"start": v(10.54, -6.57) * mm, "end": v(10.41, -6.35) * mm});
            skLineSegment(sketch, "E83.MirrorCS", {"start": v(0.13, -6.57) * mm, "end": v(0, -6.35) * mm});
            skLineSegment(sketch, "E84.MirrorCS", {"start": v(-14.73, -6.35) * mm, "end": v(-14.86, -6.57) * mm});
            skLineSegment(sketch, "E85.MirrorCS", {"start": v(-9.65, -6.35) * mm, "end": v(-9.78, -6.57) * mm});
            skLineSegment(sketch, "E86.MirrorCS", {"start": v(11.43, -6.35) * mm, "end": v(11.3, -6.57) * mm});
            skLineSegment(sketch, "E87.MirrorCS", {"start": v(11.68, -6.35) * mm, "end": v(11.56, -6.57) * mm});
            skLineSegment(sketch, "E88.MirrorCS", {"start": v(-15.24, -6.35) * mm, "end": v(-15.37, -6.57) * mm});
            skLineSegment(sketch, "E89.MirrorCS", {"start": v(-0.13, -6.57) * mm, "end": v(-0.25, -6.35) * mm});
            skLineSegment(sketch, "E90.MirrorCS", {"start": v(9.4, -6.35) * mm, "end": v(9.27, -6.57) * mm});
            skLineSegment(sketch, "E91.MirrorCS", {"start": v(14.6, -6.57) * mm, "end": v(14.48, -6.35) * mm});
            skLineSegment(sketch, "E92.MirrorCS", {"start": v(3.05, -6.35) * mm, "end": v(2.92, -6.57) * mm});
            skLineSegment(sketch, "E93.MirrorCS", {"start": v(-13.2, -6.35) * mm, "end": v(-13.34, -6.57) * mm});
            skLineSegment(sketch, "E94.MirrorCS", {"start": v(1.02, -6.35) * mm, "end": v(0.89, -6.57) * mm});
            skLineSegment(sketch, "E95.MirrorCS", {"start": v(6.6, -6.35) * mm, "end": v(6.48, -6.57) * mm});
            skLineSegment(sketch, "E96.MirrorCS", {"start": v(1.78, -6.35) * mm, "end": v(1.65, -6.57) * mm});
            skLineSegment(sketch, "E97.MirrorCS", {"start": v(-5.46, -6.57) * mm, "end": v(-5.59, -6.35) * mm});
            skLineSegment(sketch, "E98.MirrorCS", {"start": v(3.3, -6.35) * mm, "end": v(3.18, -6.57) * mm});
            skLineSegment(sketch, "E99.MirrorCS", {"start": v(-11.94, -6.35) * mm, "end": v(-12.07, -6.57) * mm});
            skLineSegment(sketch, "E100.MirrorCS", {"start": v(-12.95, -6.35) * mm, "end": v(-13.08, -6.57) * mm});
            skLineSegment(sketch, "E101.MirrorCS", {"start": v(13.59, -6.57) * mm, "end": v(13.46, -6.35) * mm});
            skLineSegment(sketch, "E102.MirrorCS", {"start": v(1.9, -6.57) * mm, "end": v(1.78, -6.35) * mm});
            skLineSegment(sketch, "E103.MirrorCS", {"start": v(-4.7, -6.57) * mm, "end": v(-4.83, -6.35) * mm});
            skLineSegment(sketch, "E104.MirrorCS", {"start": v(-3.56, -6.35) * mm, "end": v(-3.68, -6.57) * mm});
            skLineSegment(sketch, "E105.MirrorCS", {"start": v(-4.45, -6.57) * mm, "end": v(-4.57, -6.35) * mm});
            skLineSegment(sketch, "E106.MirrorCS", {"start": v(13.2, -6.35) * mm, "end": v(13.08, -6.57) * mm});
            skLineSegment(sketch, "E107.MirrorCS", {"start": v(10.67, -6.35) * mm, "end": v(10.54, -6.57) * mm});
            skLineSegment(sketch, "E108.MirrorCS", {"start": v(-7.75, -6.57) * mm, "end": v(-7.87, -6.35) * mm});
            skLineSegment(sketch, "E109.MirrorCS", {"start": v(-6.99, -6.57) * mm, "end": v(-7.11, -6.35) * mm});
            skLineSegment(sketch, "E110.MirrorCS", {"start": v(-13.08, -6.57) * mm, "end": v(-13.2, -6.35) * mm});
            skLineSegment(sketch, "E111.MirrorCS", {"start": v(10.92, -6.35) * mm, "end": v(10.8, -6.57) * mm});
            skLineSegment(sketch, "E112.MirrorCS", {"start": v(13.08, -6.57) * mm, "end": v(12.95, -6.35) * mm});
            skLineSegment(sketch, "E113.MirrorCS", {"start": v(7.62, -6.35) * mm, "end": v(7.5, -6.57) * mm});
            skLineSegment(sketch, "E114.MirrorCS", {"start": v(-8.9, -6.35) * mm, "end": v(-9.02, -6.57) * mm});
            skLineSegment(sketch, "E115.MirrorCS", {"start": v(7.37, -6.35) * mm, "end": v(7.24, -6.57) * mm});
            skLineSegment(sketch, "E116.MirrorCS", {"start": v(2.03, -6.35) * mm, "end": v(1.9, -6.57) * mm});
            skLineSegment(sketch, "E117.MirrorCS", {"start": v(-15.11, -6.57) * mm, "end": v(-15.24, -6.35) * mm});
            skLineSegment(sketch, "E118.MirrorCS", {"start": v(9.14, -6.35) * mm, "end": v(9.02, -6.57) * mm});
            skLineSegment(sketch, "E119.MirrorCS", {"start": v(-10.16, -6.35) * mm, "end": v(-10.29, -6.57) * mm});
            skLineSegment(sketch, "E120.MirrorCS", {"start": v(3.18, -6.57) * mm, "end": v(3.05, -6.35) * mm});
            skLineSegment(sketch, "E121.MirrorCS", {"start": v(-2.16, -6.57) * mm, "end": v(-2.29, -6.35) * mm});
            skLineSegment(sketch, "E122.MirrorCS", {"start": v(-13.59, -6.57) * mm, "end": v(-13.72, -6.35) * mm});
            skLineSegment(sketch, "E123.MirrorCS", {"start": v(15.62, -6.57) * mm, "end": v(15.5, -6.35) * mm});
            skLineSegment(sketch, "E124.MirrorCS", {"start": v(-15.62, -6.57) * mm, "end": v(-15.75, -6.35) * mm});
            skLineSegment(sketch, "E125.MirrorCS", {"start": v(-5.33, -6.35) * mm, "end": v(-5.46, -6.57) * mm});
            skLineSegment(sketch, "E126.MirrorCS", {"start": v(6.48, -6.57) * mm, "end": v(6.35, -6.35) * mm});
            skLineSegment(sketch, "E127.MirrorCS", {"start": v(-1.65, -6.57) * mm, "end": v(-1.78, -6.35) * mm});
            skLineSegment(sketch, "E128.MirrorCS", {"start": v(-11.05, -6.57) * mm, "end": v(-11.18, -6.35) * mm});
            skLineSegment(sketch, "E129.MirrorCS", {"start": v(-7.5, -6.57) * mm, "end": v(-7.62, -6.35) * mm});
            skLineSegment(sketch, "E130.MirrorCS", {"start": v(11.18, -6.35) * mm, "end": v(11.05, -6.57) * mm});
            skLineSegment(sketch, "E131.MirrorCS", {"start": v(-2.41, -6.57) * mm, "end": v(-2.54, -6.35) * mm});
            skLineSegment(sketch, "E132.MirrorCS", {"start": v(-11.43, -6.35) * mm, "end": v(-11.56, -6.57) * mm});
            skLineSegment(sketch, "E133.MirrorCS", {"start": v(9.27, -6.57) * mm, "end": v(9.14, -6.35) * mm});
            skLineSegment(sketch, "E134.MirrorCS", {"start": v(4.45, -6.57) * mm, "end": v(4.32, -6.35) * mm});
            skLineSegment(sketch, "E135.MirrorCS", {"start": v(4.32, -6.35) * mm, "end": v(4.2, -6.57) * mm});
            skLineSegment(sketch, "E136.MirrorCS", {"start": v(4.7, -6.57) * mm, "end": v(4.57, -6.35) * mm});
            skLineSegment(sketch, "E137.MirrorCS", {"start": v(15.24, -6.35) * mm, "end": v(15.11, -6.57) * mm});
            skLineSegment(sketch, "E138.MirrorCS", {"start": v(3.56, -6.35) * mm, "end": v(3.43, -6.57) * mm});
            skLineSegment(sketch, "E139.MirrorCS", {"start": v(-0.89, -6.57) * mm, "end": v(-1.02, -6.35) * mm});
            skLineSegment(sketch, "E140.MirrorCS", {"start": v(14.48, -6.35) * mm, "end": v(14.35, -6.57) * mm});
            skLineSegment(sketch, "E141.MirrorCS", {"start": v(-3.3, -6.35) * mm, "end": v(-3.43, -6.57) * mm});
            skLineSegment(sketch, "E142.MirrorCS", {"start": v(6.22, -6.57) * mm, "end": v(6.1, -6.35) * mm});
            skLineSegment(sketch, "E143.MirrorCS", {"start": v(-3.05, -6.35) * mm, "end": v(-3.18, -6.57) * mm});
            skLineSegment(sketch, "E144.MirrorCS", {"start": v(-7.24, -6.57) * mm, "end": v(-7.37, -6.35) * mm});
            skLineSegment(sketch, "E145.MirrorCS", {"start": v(4.06, -6.35) * mm, "end": v(3.94, -6.57) * mm});
            skLineSegment(sketch, "E146.MirrorCS", {"start": v(-4.32, -6.35) * mm, "end": v(-4.45, -6.57) * mm});
            skLineSegment(sketch, "E147.MirrorCS", {"start": v(-12.2, -6.35) * mm, "end": v(-12.32, -6.57) * mm});
            skLineSegment(sketch, "E148.MirrorCS", {"start": v(-3.81, -6.35) * mm, "end": v(-3.94, -6.57) * mm});
            skLineSegment(sketch, "E149.MirrorCS", {"start": v(-11.81, -6.57) * mm, "end": v(-11.94, -6.35) * mm});
            skLineSegment(sketch, "E150.MirrorCS", {"start": v(-12.7, -6.35) * mm, "end": v(-12.83, -6.57) * mm});
            skLineSegment(sketch, "E151.MirrorCS", {"start": v(15.11, -6.57) * mm, "end": v(14.99, -6.35) * mm});
            skLineSegment(sketch, "E152.MirrorCS", {"start": v(-0.76, -6.35) * mm, "end": v(-0.89, -6.57) * mm});
            skLineSegment(sketch, "E153.MirrorCS", {"start": v(-9.9, -6.35) * mm, "end": v(-10.03, -6.57) * mm});
            skLineSegment(sketch, "E154.MirrorCS", {"start": v(-9.14, -6.35) * mm, "end": v(-9.27, -6.57) * mm});
            skLineSegment(sketch, "E155.MirrorCS", {"start": v(-12.45, -6.35) * mm, "end": v(-12.57, -6.57) * mm});
            skLineSegment(sketch, "E156.MirrorCS", {"start": v(-14.6, -6.57) * mm, "end": v(-14.73, -6.35) * mm});
            skLineSegment(sketch, "E157.MirrorCS", {"start": v(-6.73, -6.57) * mm, "end": v(-6.86, -6.35) * mm});
            skLineSegment(sketch, "E158.MirrorCS", {"start": v(8.9, -6.35) * mm, "end": v(8.76, -6.57) * mm});
            skLineSegment(sketch, "E159.MirrorCS", {"start": v(-14.86, -6.57) * mm, "end": v(-14.99, -6.35) * mm});
            skLineSegment(sketch, "E160.MirrorCS", {"start": v(-4.2, -6.57) * mm, "end": v(-4.32, -6.35) * mm});
            skLineSegment(sketch, "E161.MirrorCS", {"start": v(-8.64, -6.35) * mm, "end": v(-8.76, -6.57) * mm});
            skLineSegment(sketch, "E162.MirrorCS", {"start": v(-6.35, -6.35) * mm, "end": v(-6.48, -6.57) * mm});
            skLineSegment(sketch, "E163.MirrorCS", {"start": v(3.94, -6.57) * mm, "end": v(3.81, -6.35) * mm});
            skLineSegment(sketch, "E164.MirrorCS", {"start": v(-5.97, -6.57) * mm, "end": v(-6.1, -6.35) * mm});
            skLineSegment(sketch, "E165.MirrorCS", {"start": v(-9.27, -6.57) * mm, "end": v(-9.4, -6.35) * mm});
            skLineSegment(sketch, "E166.MirrorCS", {"start": v(6.86, -6.35) * mm, "end": v(6.73, -6.57) * mm});
            skLineSegment(sketch, "E167.MirrorCS", {"start": v(10.41, -6.35) * mm, "end": v(10.29, -6.57) * mm});
            skLineSegment(sketch, "E168.MirrorCS", {"start": v(-10.03, -6.57) * mm, "end": v(-10.16, -6.35) * mm});
            skLineSegment(sketch, "E169.MirrorCS", {"start": v(-5.84, -6.35) * mm, "end": v(-5.97, -6.57) * mm});
            skLineSegment(sketch, "E170.MirrorCS", {"start": v(-2.67, -6.57) * mm, "end": v(-2.8, -6.35) * mm});
            skLineSegment(sketch, "E171.MirrorCS", {"start": v(8, -6.57) * mm, "end": v(7.87, -6.35) * mm});
            skLineSegment(sketch, "E172.MirrorCS", {"start": v(-4.83, -6.35) * mm, "end": v(-4.95, -6.57) * mm});
            skLineSegment(sketch, "E173.MirrorCS", {"start": v(13.84, -6.57) * mm, "end": v(13.72, -6.35) * mm});
            skLineSegment(sketch, "E174.MirrorCS", {"start": v(12.95, -6.35) * mm, "end": v(12.83, -6.57) * mm});
            skLineSegment(sketch, "E175.MirrorCS", {"start": v(8.5, -6.57) * mm, "end": v(8.38, -6.35) * mm});
            skLineSegment(sketch, "E176.MirrorCS", {"start": v(-5.59, -6.35) * mm, "end": v(-5.72, -6.57) * mm});
            skLineSegment(sketch, "E177.MirrorCS", {"start": v(7.11, -6.35) * mm, "end": v(6.99, -6.57) * mm});
            skLineSegment(sketch, "E178.MirrorCS", {"start": v(-11.3, -6.57) * mm, "end": v(-11.43, -6.35) * mm});
            skLineSegment(sketch, "E179.MirrorCS", {"start": v(4.95, -6.57) * mm, "end": v(4.83, -6.35) * mm});
            skLineSegment(sketch, "E180.MirrorCS", {"start": v(6.35, -6.35) * mm, "end": v(6.22, -6.57) * mm});
            skLineSegment(sketch, "E181.MirrorCS", {"start": v(8.76, -6.57) * mm, "end": v(8.64, -6.35) * mm});
            skLineSegment(sketch, "E182.MirrorCS", {"start": v(-9.53, -6.57) * mm, "end": v(-9.65, -6.35) * mm});
            skLineSegment(sketch, "E183.MirrorCS", {"start": v(7.24, -6.57) * mm, "end": v(7.11, -6.35) * mm});
            skLineSegment(sketch, "E184.MirrorCS", {"start": v(-4.95, -6.57) * mm, "end": v(-5.08, -6.35) * mm});
            skLineSegment(sketch, "E185.MirrorCS", {"start": v(9.02, -6.57) * mm, "end": v(8.9, -6.35) * mm});
            skLineSegment(sketch, "E186.MirrorCS", {"start": v(6.73, -6.57) * mm, "end": v(6.6, -6.35) * mm});
            skLineSegment(sketch, "E187.MirrorCS", {"start": v(6.99, -6.57) * mm, "end": v(6.86, -6.35) * mm});
            skLineSegment(sketch, "E188.MirrorCS", {"start": v(-10.54, -6.57) * mm, "end": v(-10.67, -6.35) * mm});
            skLineSegment(sketch, "E189.MirrorCS", {"start": v(-13.72, -6.35) * mm, "end": v(-13.84, -6.57) * mm});
            skLineSegment(sketch, "E190.MirrorCS", {"start": v(5.84, -6.35) * mm, "end": v(5.72, -6.57) * mm});
            skLineSegment(sketch, "E191.MirrorCS", {"start": v(5.59, -6.35) * mm, "end": v(5.46, -6.57) * mm});
            skLineSegment(sketch, "E192.MirrorCS", {"start": v(-9.78, -6.57) * mm, "end": v(-9.9, -6.35) * mm});
            skLineSegment(sketch, "E193.MirrorCS", {"start": v(-2.29, -6.35) * mm, "end": v(-2.41, -6.57) * mm});
            skLineSegment(sketch, "E194.MirrorCS", {"start": v(8.38, -6.35) * mm, "end": v(8.26, -6.57) * mm});
            skLineSegment(sketch, "E195.MirrorCS", {"start": v(-2.8, -6.35) * mm, "end": v(-2.92, -6.57) * mm});
            skLineSegment(sketch, "E196.MirrorCS", {"start": v(11.81, -6.57) * mm, "end": v(11.68, -6.35) * mm});
            skLineSegment(sketch, "E197.MirrorCS", {"start": v(12.83, -6.57) * mm, "end": v(12.7, -6.35) * mm});
            skLineSegment(sketch, "E198.MirrorCS", {"start": v(-3.94, -6.57) * mm, "end": v(-4.06, -6.35) * mm});
            skLineSegment(sketch, "E199.MirrorCS", {"start": v(15.37, -6.57) * mm, "end": v(15.24, -6.35) * mm});
            skLineSegment(sketch, "E200.MirrorCS", {"start": v(8.13, -6.35) * mm, "end": v(8, -6.57) * mm});
            skLineSegment(sketch, "E201.MirrorCS", {"start": v(-15.5, -6.35) * mm, "end": v(-15.62, -6.57) * mm});
            skLineSegment(sketch, "E202.MirrorCS", {"start": v(5.33, -6.35) * mm, "end": v(5.2, -6.57) * mm});
            skLineSegment(sketch, "E203.MirrorCS", {"start": v(-8.38, -6.35) * mm, "end": v(-8.5, -6.57) * mm});
            skLineSegment(sketch, "E204.MirrorCS", {"start": v(11.56, -6.57) * mm, "end": v(11.43, -6.35) * mm});
            skLineSegment(sketch, "E205.MirrorCS", {"start": v(-6.6, -6.35) * mm, "end": v(-6.73, -6.57) * mm});
            skLineSegment(sketch, "E206.MirrorCS", {"start": v(12.45, -6.35) * mm, "end": v(12.32, -6.57) * mm});
            skLineSegment(sketch, "E207.MirrorCS", {"start": v(-1.9, -6.57) * mm, "end": v(-2.03, -6.35) * mm});
            skLineSegment(sketch, "E208.MirrorCS", {"start": v(-10.41, -6.35) * mm, "end": v(-10.54, -6.57) * mm});
            skLineSegment(sketch, "E209.MirrorCS", {"start": v(-14.99, -6.35) * mm, "end": v(-15.11, -6.57) * mm});
            skLineSegment(sketch, "E210.MirrorCS", {"start": v(-10.67, -6.35) * mm, "end": v(-10.8, -6.57) * mm});
            skLineSegment(sketch, "E211.MirrorCS", {"start": v(14.73, -6.35) * mm, "end": v(14.6, -6.57) * mm});
            skLineSegment(sketch, "E212.MirrorCS", {"start": v(14.1, -6.57) * mm, "end": v(13.97, -6.35) * mm});
            skLineSegment(sketch, "E213.MirrorCS", {"start": v(12.2, -6.35) * mm, "end": v(12.07, -6.57) * mm});
            skLineSegment(sketch, "E214.MirrorCS", {"start": v(-15.88, -6.57) * mm, "end": v(-16, -6.35) * mm});
            skLineSegment(sketch, "E215.MirrorCS", {"start": v(-8, -6.57) * mm, "end": v(-8.13, -6.35) * mm});
            skLineSegment(sketch, "E216.MirrorCS", {"start": v(-13.34, -6.57) * mm, "end": v(-13.46, -6.35) * mm});
            skLineSegment(sketch, "E217.MirrorCS", {"start": v(4.83, -6.35) * mm, "end": v(4.7, -6.57) * mm});
            skLineSegment(sketch, "E218.MirrorCS", {"start": v(-13.46, -6.35) * mm, "end": v(-13.59, -6.57) * mm});
            skLineSegment(sketch, "E219.MirrorCS", {"start": v(5.2, -6.57) * mm, "end": v(5.08, -6.35) * mm});
            skLineSegment(sketch, "E220.MirrorCS", {"start": v(14.99, -6.35) * mm, "end": v(14.86, -6.57) * mm});
            skLineSegment(sketch, "E221.MirrorCS", {"start": v(-5.2, -6.57) * mm, "end": v(-5.33, -6.35) * mm});
            skLineSegment(sketch, "E222.MirrorCS", {"start": v(-9.02, -6.57) * mm, "end": v(-9.14, -6.35) * mm});
            skLineSegment(sketch, "E223.MirrorCS", {"start": v(-6.86, -6.35) * mm, "end": v(-6.99, -6.57) * mm});
            skLineSegment(sketch, "E224.MirrorCS", {"start": v(10.8, -6.57) * mm, "end": v(10.67, -6.35) * mm});
            skLineSegment(sketch, "E225.MirrorCS", {"start": v(-15.75, -6.35) * mm, "end": v(-15.88, -6.57) * mm});
            skLineSegment(sketch, "E226.MirrorCS", {"start": v(13.97, -6.35) * mm, "end": v(13.84, -6.57) * mm});
            skLineSegment(sketch, "E227.MirrorCS", {"start": v(10.29, -6.57) * mm, "end": v(10.16, -6.35) * mm});
            skLineSegment(sketch, "E228.MirrorCS", {"start": v(-11.68, -6.35) * mm, "end": v(-11.81, -6.57) * mm});
            skLineSegment(sketch, "E229.MirrorCS", {"start": v(-3.18, -6.57) * mm, "end": v(-3.3, -6.35) * mm});
            skLineSegment(sketch, "E230.MirrorCS", {"start": v(-6.22, -6.57) * mm, "end": v(-6.35, -6.35) * mm});
            skLineSegment(sketch, "E231.MirrorCS", {"start": v(12.07, -6.57) * mm, "end": v(11.94, -6.35) * mm});
            skLineSegment(sketch, "E232.MirrorCS", {"start": v(-15.37, -6.57) * mm, "end": v(-15.5, -6.35) * mm});
            skLineSegment(sketch, "E233.MirrorCS", {"start": v(-8.26, -6.57) * mm, "end": v(-8.38, -6.35) * mm});
            skLineSegment(sketch, "E234.MirrorCS", {"start": v(-7.11, -6.35) * mm, "end": v(-7.24, -6.57) * mm});
            skLineSegment(sketch, "E235.MirrorCS", {"start": v(5.08, -6.35) * mm, "end": v(4.95, -6.57) * mm});
            skLineSegment(sketch, "E236.MirrorCS", {"start": v(7.87, -6.35) * mm, "end": v(7.75, -6.57) * mm});
            skLineSegment(sketch, "E237.MirrorCS", {"start": v(6.1, -6.35) * mm, "end": v(5.97, -6.57) * mm});
            skLineSegment(sketch, "E238.MirrorCS", {"start": v(3.81, -6.35) * mm, "end": v(3.68, -6.57) * mm});
            skLineSegment(sketch, "E239.MirrorCS", {"start": v(-5.08, -6.35) * mm, "end": v(-5.2, -6.57) * mm});
            skLineSegment(sketch, "E240.MirrorCS", {"start": v(-8.76, -6.57) * mm, "end": v(-8.9, -6.35) * mm});
            skLineSegment(sketch, "E241.MirrorCS", {"start": v(-2.92, -6.57) * mm, "end": v(-3.05, -6.35) * mm});
            skLineSegment(sketch, "E242.MirrorCS", {"start": v(-11.56, -6.57) * mm, "end": v(-11.68, -6.35) * mm});
            skLineSegment(sketch, "E243.MirrorCS", {"start": v(15.88, -6.57) * mm, "end": v(15.75, -6.35) * mm});
            skLineSegment(sketch, "E244.MirrorCS", {"start": v(11.3, -6.57) * mm, "end": v(11.18, -6.35) * mm});
            skLineSegment(sketch, "E245.MirrorCS", {"start": v(12.32, -6.57) * mm, "end": v(12.2, -6.35) * mm});
            skLineSegment(sketch, "E246.MirrorCS", {"start": v(13.34, -6.57) * mm, "end": v(13.2, -6.35) * mm});
            skLineSegment(sketch, "E247.MirrorCS", {"start": v(12.7, -6.35) * mm, "end": v(12.57, -6.57) * mm});
            skLineSegment(sketch, "E248.MirrorCS", {"start": v(11.05, -6.57) * mm, "end": v(10.92, -6.35) * mm});
            skLineSegment(sketch, "E249.MirrorCS", {"start": v(14.86, -6.57) * mm, "end": v(14.73, -6.35) * mm});
            skLineSegment(sketch, "E250.MirrorCS", {"start": v(-1.02, -6.35) * mm, "end": v(-1.14, -6.57) * mm});
            skLineSegment(sketch, "E251.MirrorCS", {"start": v(-10.92, -6.35) * mm, "end": v(-11.05, -6.57) * mm});
            skLineSegment(sketch, "E252.MirrorCS", {"start": v(11.94, -6.35) * mm, "end": v(11.81, -6.57) * mm});
            skLineSegment(sketch, "E253.MirrorCS", {"start": v(16, -6.35) * mm, "end": v(15.88, -6.57) * mm});
            skLineSegment(sketch, "E254.MirrorCS", {"start": v(-7.87, -6.35) * mm, "end": v(-8, -6.57) * mm});
            skLineSegment(sketch, "E255.MirrorCS", {"start": v(-1.27, -6.35) * mm, "end": v(-1.4, -6.57) * mm});
            skLineSegment(sketch, "E256.MirrorCS", {"start": v(-1.78, -6.35) * mm, "end": v(-1.9, -6.57) * mm});
            skLineSegment(sketch, "E257.MirrorCS", {"start": v(16.13, -6.57) * mm, "end": v(16, -6.35) * mm});
            skLineSegment(sketch, "E258.MirrorCS", {"start": v(-12.57, -6.57) * mm, "end": v(-12.7, -6.35) * mm});
            skLineSegment(sketch, "E259.MirrorCS", {"start": v(-1.14, -6.57) * mm, "end": v(-1.27, -6.35) * mm});
            skLineSegment(sketch, "E260.MirrorCS", {"start": v(-16, -6.35) * mm, "end": v(-16.13, -6.57) * mm});
            skLineSegment(sketch, "E261.MirrorCS", {"start": v(-16.13, -6.57) * mm, "end": v(-16.26, -6.35) * mm});
            skLineSegment(sketch, "E262.MirrorCS", {"start": v(14.22, -6.35) * mm, "end": v(14.1, -6.57) * mm});
            skLineSegment(sketch, "E263.MirrorCS", {"start": v(5.97, -6.57) * mm, "end": v(5.84, -6.35) * mm});
            skLineSegment(sketch, "E264.MirrorCS", {"start": v(-1.4, -6.57) * mm, "end": v(-1.52, -6.35) * mm});
            skLineSegment(sketch, "E265.MirrorCS", {"start": v(-12.83, -6.57) * mm, "end": v(-12.95, -6.35) * mm});
            skLineSegment(sketch, "E266.MirrorCS", {"start": v(-1.52, -6.35) * mm, "end": v(-1.65, -6.57) * mm});
            skLineSegment(sketch, "E267.MirrorCS", {"start": v(4.2, -6.57) * mm, "end": v(4.06, -6.35) * mm});
            skLineSegment(sketch, "E268.MirrorCS", {"start": v(-8.13, -6.35) * mm, "end": v(-8.26, -6.57) * mm});
            skLineSegment(sketch, "E269.MirrorCS", {"start": v(2.16, -6.57) * mm, "end": v(2.03, -6.35) * mm});
            skLineSegment(sketch, "E270.MirrorCS", {"start": v(-10.8, -6.57) * mm, "end": v(-10.92, -6.35) * mm});
            skLineSegment(sketch, "E271.MirrorCS", {"start": v(8.26, -6.57) * mm, "end": v(8.13, -6.35) * mm});
            skLineSegment(sketch, "E272.MirrorCS", {"start": v(14.35, -6.57) * mm, "end": v(14.22, -6.35) * mm});
            skLineSegment(sketch, "E273.MirrorCS", {"start": v(16.26, -6.1) * mm, "end": v(16.26, -6.35) * mm});
            skLineSegment(sketch, "E274.MirrorCS", {"start": v(-16.26, -6.1) * mm, "end": v(16.26, -6.1) * mm});
            skLineSegment(sketch, "E275.MirrorCS", {"start": v(-16.26, -6.35) * mm, "end": v(-16.26, -6.1) * mm});
            skLineSegment(sketch, "E276.MirrorCS", {"start": v(16.26, -6.35) * mm, "end": v(16.13, -6.57) * mm});
            skSolve(sketch);
        }
        {
            var Q0;
            Q0 = qSketchRegion(id + "F2", true);
            extrude(context, id + "F3", {"entities" : qUnion([Q0]), "operationType" : NewBodyOperationType.REMOVE, "endBound" : BoundingType.SYMMETRIC, "oppositeDirection" : true, "depth" : 25.4 * mm, "offsetDistance" : 25.4 * mm});
        }
        {
            var Q0;
            Q0=makeQuery(id+"F1.opExtrude","SWEPT_EDGE",EDGE,{"disambiguationData":[OSD([sQuery(id+"F0.wireOp",EDGE,"E0.top"),sQuery(id+"F0.wireOp",EDGE,"E3.trimOffspring")])]});
            var Q1;
            Q1=makeQuery(id+"F1.opExtrude","SWEPT_EDGE",EDGE,{"disambiguationData":[OSD([sQuery(id+"F0.wireOp",EDGE,"E0.top"),sQuery(id+"F0.wireOp",EDGE,"E2.trimOffspring")])]});
            var Q2;
            Q2=makeQuery(id+"F1.opExtrude","SWEPT_EDGE",EDGE,{"disambiguationData":[OSD([sQuery(id+"F0.wireOp",EDGE,"E0.bottom"),sQuery(id+"F0.wireOp",EDGE,"E0.left")])]});
            var Q3;
            Q3=makeQuery(id+"F1.opExtrude","SWEPT_EDGE",EDGE,{"disambiguationData":[OSD([sQuery(id+"F0.wireOp",EDGE,"E0.bottom"),sQuery(id+"F0.wireOp",EDGE,"E0.right")])]});
            fillet(context, id + "F4", {"entities" : qUnion([Q0, Q1, Q2, Q3]), "radius" : 5.08 * mm, "tangentPropagation" : true, "allowEdgeOverflow" : false});
        }
        {
            var Q0;
            Q0=makeQuery(id+"F1.opExtrude","CAP_EDGE",EDGE,{"disambiguationData":[OSD([sQuery(id+"F0.wireOp",EDGE,"E0.top")])],"isStart":false});
            var Q1;
            Q1=makeQuery(id+"F1.opExtrude","CAP_EDGE",EDGE,{"disambiguationData":[OSD([sQuery(id+"F0.wireOp",EDGE,"E0.top")])],"isStart":true});
            var Q2;
            Q2=makeQuery(id+"F1.opExtrude","CAP_EDGE",EDGE,{"disambiguationData":[OSD([sQuery(id+"F0.wireOp",EDGE,"E0.bottom")])],"isStart":false});
            var Q3;
            Q3=makeQuery(id+"F1.opExtrude","CAP_EDGE",EDGE,{"disambiguationData":[OSD([sQuery(id+"F0.wireOp",EDGE,"E0.bottom")])],"isStart":true});
            fillet(context, id + "F5", {"entities" : qUnion([Q0, Q1, Q2, Q3]), "radius" : 0.5 * mm, "tangentPropagation" : true, "allowEdgeOverflow" : false});
        }
    });
